FCSTD DOCUMENT  (FreeCAD 1.0R39319 (Git))
Label: sketch3
License: All rights reserved
LicenseURL: https://en.wikipedia.org/wiki/All_rights_reserved
objects: PartDesign::Body×2, Sketcher::SketchObject×1
note: 4 computed .brp shape members not serialized (recipe doc carries the construction recipe); baked Part::Feature solids carry a one-line shape summary decoded from their .brp

FEATURE [PartDesign::Body] Body
  AllowCompound = false
  Origin = -> Origin
FEATURE [Sketcher::SketchObject] Sketch
  ArcFitTolerance = 1e-06
  AttachmentSupport = -> [XY_Plane001]
  FullyConstrained = true
  MakeInternals = false
  MapMode = 5
  sketch-geometry (14):
    g0: Circle CenterX=0 CenterY=70 CenterZ=0 NormalX=0 NormalY=0 NormalZ=1 AngleXU=0 Radius=30
    g1: Circle [constr] CenterX=0 CenterY=70 CenterZ=0 NormalX=0 NormalY=0 NormalZ=1 AngleXU=0 Radius=20
    g2: Circle CenterX=0.063454 CenterY=89.9999 CenterZ=0 NormalX=0 NormalY=0 NormalZ=1 AngleXU=0 Radius=5
    g3: Circle CenterX=0.063454 CenterY=50.0001 CenterZ=0 NormalX=0 NormalY=0 NormalZ=1 AngleXU=0 Radius=5
    g4: Circle CenterX=-19.9999 CenterY=70.0527 CenterZ=0 NormalX=0 NormalY=0 NormalZ=1 AngleXU=0 Radius=5
    g5: Circle CenterX=19.9999 CenterY=70.0527 CenterZ=0 NormalX=0 NormalY=0 NormalZ=1 AngleXU=0 Radius=5
    g6: Circle CenterX=40 CenterY=0 CenterZ=0 NormalX=0 NormalY=0 NormalZ=1 AngleXU=0 Radius=15
    g7: Circle CenterX=-40 CenterY=0 CenterZ=0 NormalX=0 NormalY=0 NormalZ=1 AngleXU=0 Radius=15
    g8: Circle CenterX=-40 CenterY=0 CenterZ=0 NormalX=0 NormalY=0 NormalZ=1 AngleXU=0 Radius=10
    g9: Circle CenterX=40 CenterY=0 CenterZ=0 NormalX=0 NormalY=0 NormalZ=1 AngleXU=0 Radius=10
    g10: LineSegment StartX=-28.3617 StartY=79.7781 StartZ=0 EndX=-54.1809 EndY=4.88907 EndZ=0
    g11: LineSegment StartX=28.3617 StartY=79.7781 StartZ=0 EndX=54.1809 EndY=4.88907 EndZ=0
    g12: ArcOfCircle CenterX=-0.527356 CenterY=-62.7914 CenterZ=0 NormalX=0 NormalY=0 NormalZ=1 AngleXU=0 Radius=60 StartAngle=1.03962 EndAngle=2.05813
    g13: Circle CenterX=0 CenterY=70 CenterZ=0 NormalX=0 NormalY=0 NormalZ=1 AngleXU=0 Radius=8
  constraints (37):
    c: PointOnObject(g0,g-2)
    c: Diameter(g0) = 60
    c: Diameter(g1) = 40
    c: Coincident(g1,g0)
    c: Diameter(g2) = 10
    c: PointOnObject(g2,g1)
    c: PointOnObject(g3,g1)
    c: PointOnObject(g4,g1)
    c: PointOnObject(g5,g1)
    c: Equal(g2,g4)
    c: Equal(g4,g3)
    c: Equal(g3,g5)
    c: PointOnObject(g6,g-1)
    c: PointOnObject(g7,g-1)
    c: Diameter(g6) = 30
    c: Equal(g6,g7)
    c: DistanceX(g7,g6) = 80
    c: DistanceX(g0,g6) = 40
    c: DistanceY(g6,g0) = 70
    c: Diameter(g8) = 20
    c: Coincident(g8,g7)
    c: Diameter(g9) = 20
    c: Coincident(g9,g6)
    c: Tangent(g10,g0) = -1.5708
    c: Tangent(g10,g7) = -1.5708
    c: PointOnObject(g12,g6)
    c: PointOnObject(g12,g7)
    c: Radius(g12) = 60
    c: Horizontal(g4,g5)
    c: Block(g11)
    c: Block(g12)
    c: Diameter(g13) = 16
    c: Coincident(g13,g0)
    c: Vertical(g2,g3)
    c: Block(g3)
    c: Block(g2)
    c: Block(g4)
FEATURE [PartDesign::Body] Body001
  AllowCompound = false
  Group = -> [Sketch]
  Origin = -> Origin001
